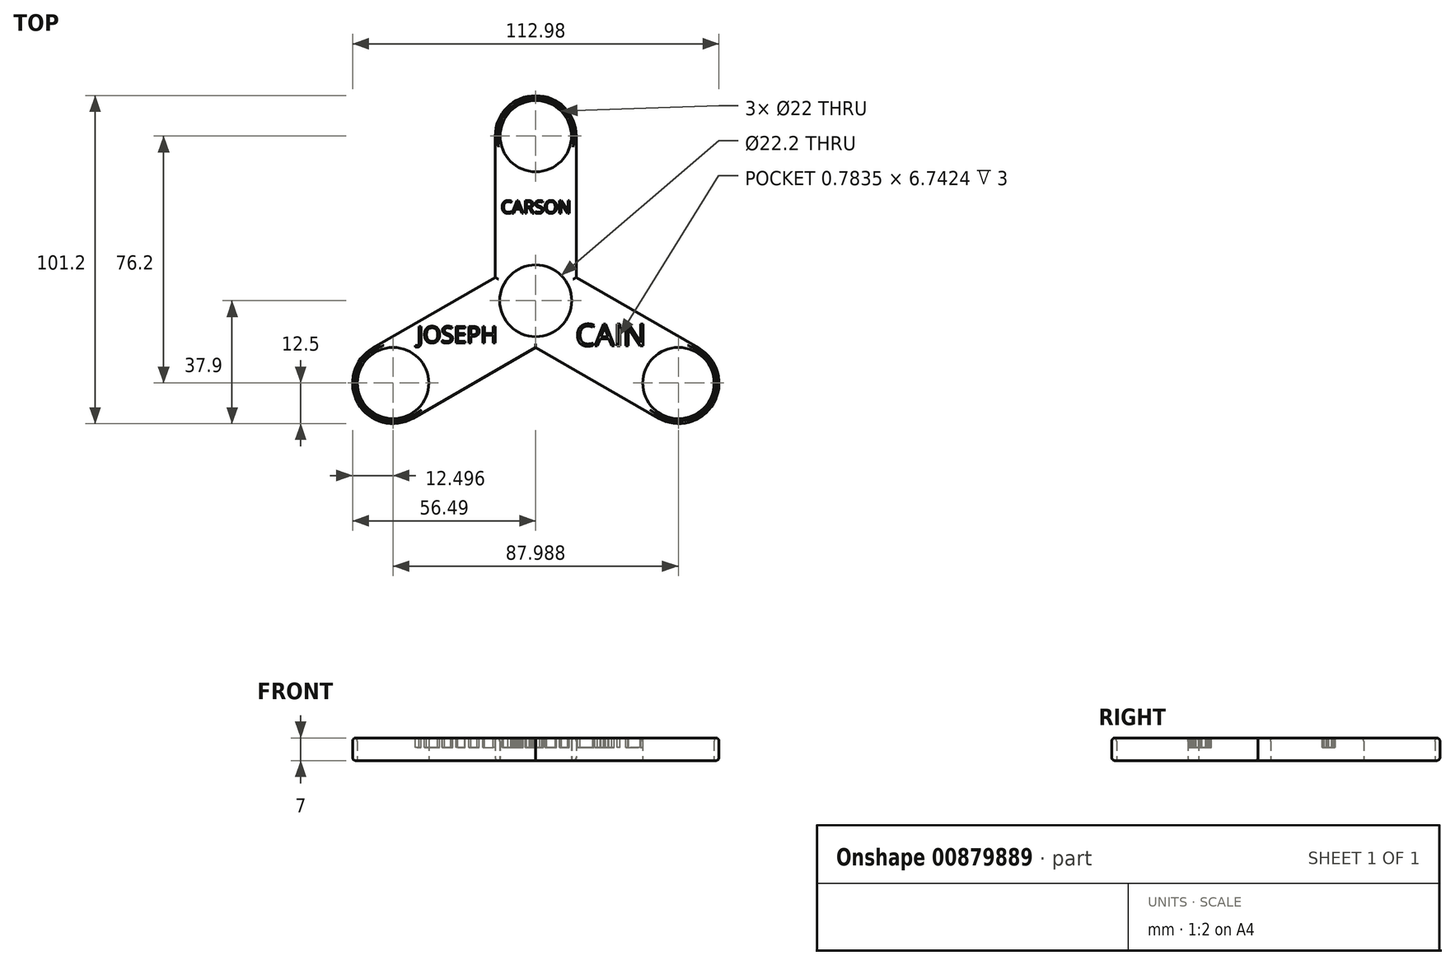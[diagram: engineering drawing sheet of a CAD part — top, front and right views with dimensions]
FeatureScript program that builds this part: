
annotation { "Feature Type Name" : "Feature", "Feature Type Description" : "" }
export const myFeature = defineFeature(function(context is Context, id is Id, definition is map)
    precondition{}
    {
        {
            var Q0;
            Q0=qCreatedBy(makeId("Top.planeOp"),FACE);
            var sketch = newSketch(context, id + "F0", { "sketchPlane" : qUnion([Q0])});
            skLineSegment(sketch, "E0", {"start": v(-12.5, 50.8) * mm, "end": v(-12.5, 7.22) * mm});
            skLineSegment(sketch, "E1", {"start": v(12.5, 50.8) * mm, "end": v(12.5, 0) * mm});
            skArc(sketch, "E2", {"start": v(12.5, 50.8) * mm, "mid": v(0, 63.3) * mm, "end": v(-12.5, 50.8) * mm});
            skLineSegment(sketch, "E3.1.0", {"start": v(-37.74, -36.23) * mm, "end": v(0, -14.43) * mm});
            skArc(sketch, "E3.1.1", {"start": v(-50.24, -14.57) * mm, "mid": v(-54.82, -31.65) * mm, "end": v(-37.74, -36.23) * mm});
            skLineSegment(sketch, "E3.1.2", {"start": v(-50.24, -14.57) * mm, "end": v(-12.5, 7.22) * mm});
            skLineSegment(sketch, "E3.2.0", {"start": v(50.24, -14.57) * mm, "end": v(12.5, 7.22) * mm});
            skArc(sketch, "E3.2.1", {"start": v(37.74, -36.23) * mm, "mid": v(54.82, -31.65) * mm, "end": v(50.24, -14.57) * mm});
            skLineSegment(sketch, "E3.2.2", {"start": v(37.74, -36.23) * mm, "end": v(0, -14.43) * mm});
            skPoint(sketch, "E3.center", {"position": v(0, 0) * mm});
            skPoint(sketch, "E4.orphan", {"position": v(-6.25, 10.83) * mm});
            skPoint(sketch, "E5.orphan", {"position": v(-12.5, 0) * mm});
            skPoint(sketch, "E6.orphan", {"position": v(6.25, 10.83) * mm});
            skPoint(sketch, "E7.orphan", {"position": v(6.25, -10.83) * mm});
            skPoint(sketch, "E8.orphan", {"position": v(-6.25, -10.83) * mm});
            skSolve(sketch);
        }
        {
            var Q0;
            Q0=qCreatedBy(makeId("Top.planeOp"),FACE);
            var sketch = newSketch(context, id + "F1", { "sketchPlane" : qUnion([Q0])});
            skCircle(sketch, "E9", {"center": v(0, 50.8) * mm, "radius": 11 * mm});
            skCircle(sketch, "E10.1.0", {"center": v(-44, -25.4) * mm, "radius": 11 * mm});
            skCircle(sketch, "E10.2.0", {"center": v(44, -25.4) * mm, "radius": 11 * mm});
            skPoint(sketch, "E10.center", {"position": v(0, 0) * mm});
            skCircle(sketch, "E11", {"center": v(0, 0) * mm, "radius": 11.1 * mm});
            skSolve(sketch);
        }
        {
            var Q0;
            Q0=qSketchRegion(id+"F0",true);
            extrude(context, id + "F2", {"entities" : qUnion([Q0]), "depth" : 7 * mm, "offsetDistance" : 25.4 * mm});
        }
        {
            var Q0;
            Q0=qSketchRegion(id+"F1",true);
            extrude(context, id + "F3", {"entities" : qUnion([Q0]), "operationType" : NewBodyOperationType.REMOVE, "depth" : 25.4 * mm, "offsetDistance" : 25.4 * mm});
        }
        {
            var Q0;
            Q0=makeQuery(id+"F3.boolean.opBoolean","INTERSECT",EDGE,{"derivedFrom":[makeQuery(id+"F2.opExtrude","CAP_FACE",FACE,{"disambiguationData":[OSD([sQuery(id+"F0.wireOp",EDGE,"E0"),sQuery(id+"F0.wireOp",EDGE,"E1"),sQuery(id+"F0.wireOp",EDGE,"E2"),sQuery(id+"F0.wireOp",EDGE,"E3.1.0"),sQuery(id+"F0.wireOp",EDGE,"E3.1.1"),sQuery(id+"F0.wireOp",EDGE,"E3.1.2"),sQuery(id+"F0.wireOp",EDGE,"E3.2.0"),sQuery(id+"F0.wireOp",EDGE,"E3.2.1"),sQuery(id+"F0.wireOp",EDGE,"E3.2.2")])],"isStart":false}),makeQuery(id+"F3.opExtrude","SWEPT_FACE",FACE,{"disambiguationData":[OSD([sQuery(id+"F1.wireOp",EDGE,"E9")])]})]});
            var Q1;
            Q1=makeQuery(id+"F3.boolean.opBoolean","COPY",EDGE,{"derivedFrom":makeQuery(id+"F3.opExtrude","CAP_EDGE",EDGE,{"disambiguationData":[OSD([sQuery(id+"F1.wireOp",EDGE,"E9")])],"isStart":true})});
            var Q2;
            Q2=makeQuery(id+"F2.opExtrude","CAP_EDGE",EDGE,{"disambiguationData":[OSD([sQuery(id+"F0.wireOp",EDGE,"E0")])],"isStart":true});
            var Q3;
            Q3=makeQuery(id+"F2.opExtrude","CAP_EDGE",EDGE,{"disambiguationData":[OSD([sQuery(id+"F0.wireOp",EDGE,"E1")])],"isStart":true});
            var Q4;
            Q4=makeQuery(id+"F2.opExtrude","CAP_EDGE",EDGE,{"disambiguationData":[OSD([sQuery(id+"F0.wireOp",EDGE,"E1")])],"isStart":false});
            var Q5;
            Q5=makeQuery(id+"F2.opExtrude","CAP_EDGE",EDGE,{"disambiguationData":[OSD([sQuery(id+"F0.wireOp",EDGE,"E3.1.2")])],"isStart":true});
            var Q6;
            Q6=makeQuery(id+"F2.opExtrude","CAP_EDGE",EDGE,{"disambiguationData":[OSD([sQuery(id+"F0.wireOp",EDGE,"E3.1.2")])],"isStart":false});
            var Q7;
            Q7=makeQuery(id+"F3.boolean.opBoolean","COPY",EDGE,{"derivedFrom":makeQuery(id+"F3.opExtrude","CAP_EDGE",EDGE,{"disambiguationData":[OSD([sQuery(id+"F1.wireOp",EDGE,"E10.1.0")])],"isStart":true})});
            var Q8;
            Q8=makeQuery(id+"F3.boolean.opBoolean","INTERSECT",EDGE,{"derivedFrom":[makeQuery(id+"F2.opExtrude","CAP_FACE",FACE,{"disambiguationData":[OSD([sQuery(id+"F0.wireOp",EDGE,"E0"),sQuery(id+"F0.wireOp",EDGE,"E1"),sQuery(id+"F0.wireOp",EDGE,"E2"),sQuery(id+"F0.wireOp",EDGE,"E3.1.0"),sQuery(id+"F0.wireOp",EDGE,"E3.1.1"),sQuery(id+"F0.wireOp",EDGE,"E3.1.2"),sQuery(id+"F0.wireOp",EDGE,"E3.2.0"),sQuery(id+"F0.wireOp",EDGE,"E3.2.1"),sQuery(id+"F0.wireOp",EDGE,"E3.2.2")])],"isStart":false}),makeQuery(id+"F3.opExtrude","SWEPT_FACE",FACE,{"disambiguationData":[OSD([sQuery(id+"F1.wireOp",EDGE,"E10.1.0")])]})]});
            var Q9;
            Q9=makeQuery(id+"F2.opExtrude","CAP_EDGE",EDGE,{"disambiguationData":[OSD([sQuery(id+"F0.wireOp",EDGE,"E3.2.0")])],"isStart":false});
            var Q10;
            Q10=makeQuery(id+"F2.opExtrude","CAP_EDGE",EDGE,{"disambiguationData":[OSD([sQuery(id+"F0.wireOp",EDGE,"E3.2.2")])],"isStart":false});
            var Q11;
            Q11=makeQuery(id+"F3.boolean.opBoolean","INTERSECT",EDGE,{"derivedFrom":[makeQuery(id+"F2.opExtrude","CAP_FACE",FACE,{"disambiguationData":[OSD([sQuery(id+"F0.wireOp",EDGE,"E0"),sQuery(id+"F0.wireOp",EDGE,"E1"),sQuery(id+"F0.wireOp",EDGE,"E2"),sQuery(id+"F0.wireOp",EDGE,"E3.1.0"),sQuery(id+"F0.wireOp",EDGE,"E3.1.1"),sQuery(id+"F0.wireOp",EDGE,"E3.1.2"),sQuery(id+"F0.wireOp",EDGE,"E3.2.0"),sQuery(id+"F0.wireOp",EDGE,"E3.2.1"),sQuery(id+"F0.wireOp",EDGE,"E3.2.2")])],"isStart":false}),makeQuery(id+"F3.opExtrude","SWEPT_FACE",FACE,{"disambiguationData":[OSD([sQuery(id+"F1.wireOp",EDGE,"E10.2.0")])]})]});
            var Q12;
            Q12=makeQuery(id+"F3.boolean.opBoolean","COPY",EDGE,{"derivedFrom":makeQuery(id+"F3.opExtrude","CAP_EDGE",EDGE,{"disambiguationData":[OSD([sQuery(id+"F1.wireOp",EDGE,"E10.2.0")])],"isStart":true})});
            var Q13;
            Q13=makeQuery(id+"F2.opExtrude","CAP_EDGE",EDGE,{"disambiguationData":[OSD([sQuery(id+"F0.wireOp",EDGE,"E3.2.2")])],"isStart":true});
            var Q14;
            Q14=makeQuery(id+"F2.opExtrude","CAP_EDGE",EDGE,{"disambiguationData":[OSD([sQuery(id+"F0.wireOp",EDGE,"E3.2.0")])],"isStart":true});
            fillet(context, id + "F4", {"entities" : qUnion([Q0, Q1, Q2, Q3, Q4, Q5, Q6, Q7, Q8, Q9, Q10, Q11, Q12, Q13, Q14]), "radius" : 1 * mm, "tangentPropagation" : true, "allowEdgeOverflow" : false});
        }
        {
            var Q0;
            Q0=makeQuery(id+"F3.boolean.opBoolean","INTERSECT",EDGE,{"derivedFrom":[makeQuery(id+"F2.opExtrude","CAP_FACE",FACE,{"disambiguationData":[OSD([sQuery(id+"F0.wireOp",EDGE,"E0"),sQuery(id+"F0.wireOp",EDGE,"E1"),sQuery(id+"F0.wireOp",EDGE,"E2"),sQuery(id+"F0.wireOp",EDGE,"E3.1.0"),sQuery(id+"F0.wireOp",EDGE,"E3.1.1"),sQuery(id+"F0.wireOp",EDGE,"E3.1.2"),sQuery(id+"F0.wireOp",EDGE,"E3.2.0"),sQuery(id+"F0.wireOp",EDGE,"E3.2.1"),sQuery(id+"F0.wireOp",EDGE,"E3.2.2")])],"isStart":false}),makeQuery(id+"F3.opExtrude","SWEPT_FACE",FACE,{"disambiguationData":[OSD([sQuery(id+"F1.wireOp",EDGE,"E11")])]})]});
            var Q1;
            Q1=makeQuery(id+"F3.boolean.opBoolean","COPY",EDGE,{"derivedFrom":makeQuery(id+"F3.opExtrude","CAP_EDGE",EDGE,{"disambiguationData":[OSD([sQuery(id+"F1.wireOp",EDGE,"E11")])],"isStart":true})});
            fillet(context, id + "F5", {"entities" : qUnion([Q0, Q1]), "radius" : 1 * mm, "tangentPropagation" : true, "allowEdgeOverflow" : false});
        }
        {
            var Q0;
            Q0=makeQuery(id+"F2.opExtrude","CAP_FACE",FACE,{"disambiguationData":[OSD([sQuery(id+"F0.wireOp",EDGE,"E0"),sQuery(id+"F0.wireOp",EDGE,"E1"),sQuery(id+"F0.wireOp",EDGE,"E2"),sQuery(id+"F0.wireOp",EDGE,"E3.1.0"),sQuery(id+"F0.wireOp",EDGE,"E3.1.1"),sQuery(id+"F0.wireOp",EDGE,"E3.1.2"),sQuery(id+"F0.wireOp",EDGE,"E3.2.0"),sQuery(id+"F0.wireOp",EDGE,"E3.2.1"),sQuery(id+"F0.wireOp",EDGE,"E3.2.2")])],"isStart":false});
            var sketch = newSketch(context, id + "F6", { "sketchPlane" : qUnion([Q0])});
            skText(sketch, "E12", { "text": "CARSON", "fontName": "OpenSans-Regular.ttf"});
            skPoint(sketch, "E13", {"position": v(11.5, 27) * mm});
            const initialGuessF6  = {"E12": [-0.01071, 0.027, 1, 0, 0.00393]};
            skSetInitialGuess(sketch, initialGuessF6);
            skSolve(sketch);
        }
        {
            var Q0;
            Q0 = qSketchRegion(id + "F6", true);
            extrude(context, id + "F7", {"entities" : qUnion([Q0]), "operationType" : NewBodyOperationType.REMOVE, "oppositeDirection" : true, "depth" : 3 * mm, "offsetDistance" : 25 * mm});
        }
        {
            var Q0;
            {var subQ0=sQuery(id+"F0.wireOp",EDGE,"E3.2.2");var subQ1=sQuery(id+"F0.wireOp",EDGE,"E3.2.1");var subQ2=sQuery(id+"F0.wireOp",EDGE,"E3.2.0");var subQ3=sQuery(id+"F0.wireOp",EDGE,"E3.1.2");var subQ4=sQuery(id+"F0.wireOp",EDGE,"E3.1.1");var subQ5=sQuery(id+"F0.wireOp",EDGE,"E3.1.0");var subQ6=sQuery(id+"F0.wireOp",EDGE,"E2");var subQ7=sQuery(id+"F0.wireOp",EDGE,"E1");var subQ8=sQuery(id+"F0.wireOp",EDGE,"E0");Q0=makeQuery(id+"F7.boolean.opBoolean","SPLIT",FACE,{"disambiguationData":[TD([makeQuery(id+"F7.opExtrude","SWEPT_FACE",FACE,{"disambiguationData":[OSD([sQuery(id+"F6.wireOp",EDGE,"E12.sketch_text.stroke-0")])]})])],"derivedFrom":makeQuery(id+"F2.opExtrude","CAP_FACE",FACE,{"disambiguationData":[OSD([subQ8,subQ7,subQ6,subQ5,subQ4,subQ3,subQ2,subQ1,subQ0])],"isStart":false})});}
            var sketch = newSketch(context, id + "F8", { "sketchPlane" : qUnion([Q0])});
            skText(sketch, "E14", { "text": "JOSEPH", "fontName": "OpenSans-Regular.ttf"});
            const initialGuessF8  = {"E14": [-0.03663, -0.01299, 1, 0, 0.00512]};
            skSetInitialGuess(sketch, initialGuessF8);
            skSolve(sketch);
        }
        {
            var Q0;
            Q0 = qSketchRegion(id + "F8", true);
            extrude(context, id + "F9", {"entities" : qUnion([Q0]), "operationType" : NewBodyOperationType.REMOVE, "oppositeDirection" : true, "depth" : 3 * mm, "offsetDistance" : 25 * mm});
        }
        {
            var Q0;
            {var subQ51=sQuery(id+"F0.wireOp",EDGE,"E1");var subQ56=sQuery(id+"F0.wireOp",EDGE,"E3.1.2");var subQ59=makeQuery(id+"F7.opExtrude","SWEPT_FACE",FACE,{"disambiguationData":[OSD([sQuery(id+"F6.wireOp",EDGE,"E12.sketch_text.stroke-0")])]});var subQ60=sQuery(id+"F0.wireOp",EDGE,"E3.2.2");var subQ61=sQuery(id+"F0.wireOp",EDGE,"E3.2.1");var subQ62=sQuery(id+"F0.wireOp",EDGE,"E3.2.0");var subQ63=sQuery(id+"F0.wireOp",EDGE,"E3.1.1");var subQ64=sQuery(id+"F0.wireOp",EDGE,"E3.1.0");var subQ65=sQuery(id+"F0.wireOp",EDGE,"E2");var subQ66=sQuery(id+"F0.wireOp",EDGE,"E0");Q0=makeQuery(id+"F9.boolean.opBoolean","SPLIT",FACE,{"disambiguationData":[TD([makeQuery(id+"F7.boolean.opBoolean","COPY",FACE,{"derivedFrom":subQ59})])],"derivedFrom":makeQuery(id+"F7.boolean.opBoolean","SPLIT",FACE,{"disambiguationData":[TD([subQ59])],"derivedFrom":makeQuery(id+"F2.opExtrude","CAP_FACE",FACE,{"disambiguationData":[OSD([subQ66,subQ51,subQ65,subQ64,subQ63,subQ56,subQ62,subQ61,subQ60])],"isStart":false})})});}
            var sketch = newSketch(context, id + "F10", { "sketchPlane" : qUnion([Q0])});
            skText(sketch, "E15", { "text": "CAIN", "fontName": "OpenSans-Regular.ttf"});
            const initialGuessF10  = {"E15": [0.01228, -0.01395, 1, 0, 0.0068]};
            skSetInitialGuess(sketch, initialGuessF10);
            skSolve(sketch);
        }
        {
            var Q0;
            Q0 = qSketchRegion(id + "F10", true);
            extrude(context, id + "F11", {"entities" : qUnion([Q0]), "operationType" : NewBodyOperationType.REMOVE, "oppositeDirection" : true, "depth" : 3 * mm, "offsetDistance" : 25 * mm});
        }
    });
